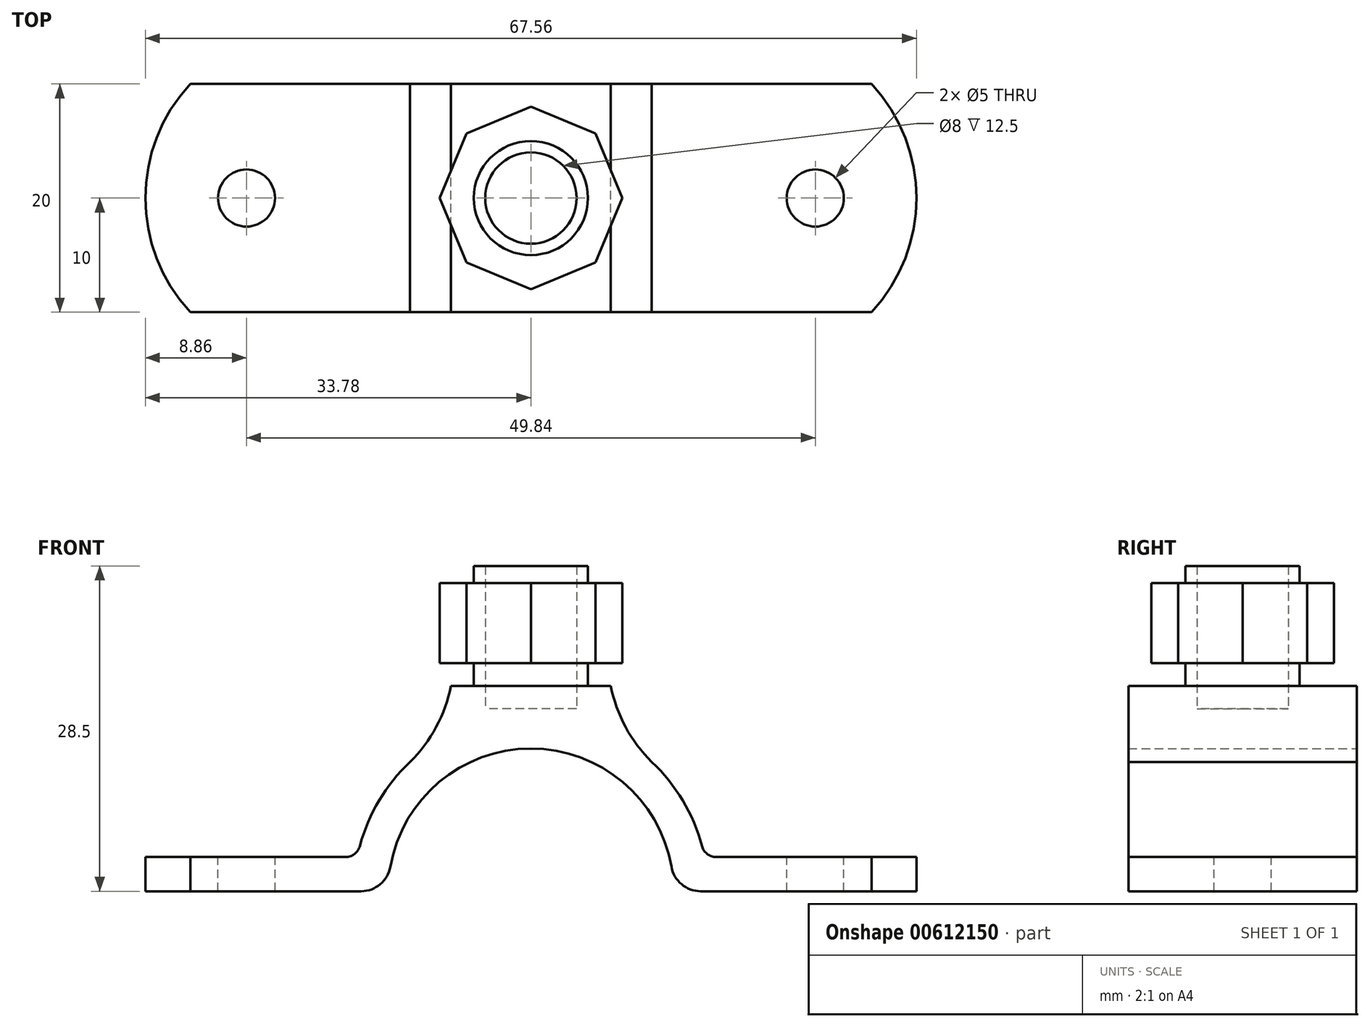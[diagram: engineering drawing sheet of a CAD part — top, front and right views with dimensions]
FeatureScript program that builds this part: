
annotation { "Feature Type Name" : "Feature", "Feature Type Description" : "" }
export const myFeature = defineFeature(function(context is Context, id is Id, definition is map)
    precondition{}
    {
        {
            var Q0;
            Q0=qCreatedBy(makeId("Front.planeOp"),FACE);
            var sketch = newSketch(context, id + "F0", { "sketchPlane" : qUnion([Q0])});
            skArc(sketch, "E0", {"start": v(-10.6, 11.32) * mm, "mid": v(-13.3, 7.95) * mm, "end": v(-14.98, 3.97) * mm});
            skArc(sketch, "E1.0", {"start": v(12.31, 2.15) * mm, "mid": v(0, 12.5) * mm, "end": v(-12.31, 2.15) * mm});
            skLineSegment(sketch, "E2", {"start": v(-14.87, 0) * mm, "end": v(-29.85, 0) * mm});
            skLineSegment(sketch, "E3", {"start": v(-29.85, 0) * mm, "end": v(-29.85, 3) * mm});
            skLineSegment(sketch, "E4", {"start": v(-29.85, 3) * mm, "end": v(-16.24, 3) * mm});
            skLineSegment(sketch, "E5", {"start": v(14.87, 0) * mm, "end": v(29.85, 0) * mm});
            skLineSegment(sketch, "E6", {"start": v(29.85, 0) * mm, "end": v(29.85, 3) * mm});
            skLineSegment(sketch, "E7", {"start": v(29.85, 3) * mm, "end": v(16.24, 3) * mm});
            skLineSegment(sketch, "E8", {"start": v(0, 0) * mm, "end": v(0, 18) * mm, "construction": true});
            skLineSegment(sketch, "E9", {"start": v(-7, 18) * mm, "end": v(7, 18) * mm});
            skArc(sketch, "E10", {"start": v(-10.6, 11.32) * mm, "mid": v(-8.3, 14.4) * mm, "end": v(-7, 18) * mm});
            skArc(sketch, "E11", {"start": v(7, 18) * mm, "mid": v(8.3, 14.4) * mm, "end": v(10.6, 11.32) * mm});
            skArc(sketch, "E12.trimOffspring", {"start": v(14.98, 3.97) * mm, "mid": v(13.3, 7.95) * mm, "end": v(10.6, 11.32) * mm});
            skPoint(sketch, "E13.visualSharp", {"position": v(-15.2, 3) * mm});
            skArc(sketch, "E13.filletArc", {"start": v(-16.24, 3) * mm, "mid": v(-15.45, 3.27) * mm, "end": v(-14.98, 3.97) * mm});
            skPoint(sketch, "E14.visualSharp", {"position": v(15.2, 3) * mm});
            skArc(sketch, "E14.filletArc", {"start": v(14.98, 3.97) * mm, "mid": v(15.45, 3.27) * mm, "end": v(16.24, 3) * mm});
            skPoint(sketch, "E15.visualSharp", {"position": v(-12.5, 0) * mm});
            skArc(sketch, "E15.filletArc", {"start": v(-14.87, 0) * mm, "mid": v(-13.2, 0.6) * mm, "end": v(-12.31, 2.15) * mm});
            skPoint(sketch, "E16.visualSharp", {"position": v(12.5, 0) * mm});
            skArc(sketch, "E16.filletArc", {"start": v(12.31, 2.15) * mm, "mid": v(13.2, 0.6) * mm, "end": v(14.87, 0) * mm});
            skSolve(sketch);
        }
        {
            var Q0;
            Q0=makeQuery(id+"F0.imprint","IMPRINT",FACE,{"disambiguationData":[TD([[makeQuery(id+"F0.imprint","IMPRINT",EDGE,{"derivedFrom":sQuery(id+"F0.wireOp",EDGE,"E0")}),1.0]])]});
            extrude(context, id + "F1", {"entities" : qUnion([Q0]), "endBound" : BoundingType.SYMMETRIC, "depth" : 20 * mm, "offsetDistance" : 25 * mm});
        }
        {
            var Q0;
            Q0=makeQuery(id+"F1.opExtrude","SWEPT_FACE",FACE,{"disambiguationData":[OSD([sQuery(id+"F0.wireOp",EDGE,"E4")])]});
            var sketch = newSketch(context, id + "F2", { "sketchPlane" : qUnion([Q0])});
            skCircle(sketch, "E17", {"center": v(-24.92, 0) * mm, "radius": 2.5 * mm});
            skCircle(sketch, "E18", {"center": v(24.92, 0) * mm, "radius": 2.5 * mm});
            skSolve(sketch);
        }
        {
            var Q0;
            Q0=makeQuery(id+"F2.imprint","IMPRINT",FACE,{"disambiguationData":[TD([[makeQuery(id+"F2.imprint","IMPRINT",EDGE,{"derivedFrom":sQuery(id+"F2.wireOp",EDGE,"E17")}),1.0]])]});
            var Q1;
            Q1=makeQuery(id+"F2.imprint","IMPRINT",FACE,{"disambiguationData":[TD([[makeQuery(id+"F2.imprint","IMPRINT",EDGE,{"derivedFrom":sQuery(id+"F2.wireOp",EDGE,"E18")}),1.0]])]});
            extrude(context, id + "F3", {"entities" : qUnion([Q0, Q1]), "operationType" : NewBodyOperationType.REMOVE, "oppositeDirection" : true, "depth" : 25 * mm, "offsetDistance" : 25 * mm});
        }
        {
            var Q0;
            Q0=makeQuery(id+"F1.opExtrude","SWEPT_FACE",FACE,{"disambiguationData":[OSD([sQuery(id+"F0.wireOp",EDGE,"E4")])]});
            var sketch = newSketch(context, id + "F4", { "sketchPlane" : qUnion([Q0])});
            skArc(sketch, "E19", {"start": v(-29.85, 10) * mm, "mid": v(-33.78, 0) * mm, "end": v(-29.85, -10) * mm});
            skSolve(sketch);
        }
        {
            var Q0;
            Q0=makeQuery(id+"F4.imprint","IMPRINT",FACE,{"disambiguationData":[TD([[makeQuery(id+"F4.imprint","IMPRINT",EDGE,{"derivedFrom":sQuery(id+"F4.wireOp",EDGE,"E19")}),1.0]])]});
            var Q1;
            Q1=makeQuery(id+"F1.opExtrude","SWEPT_FACE",FACE,{"disambiguationData":[OSD([sQuery(id+"F0.wireOp",EDGE,"E2")])]});
            extrude(context, id + "F5", {"entities" : qUnion([Q0]), "operationType" : NewBodyOperationType.ADD, "endBound" : BoundingType.UP_TO_SURFACE, "oppositeDirection" : true, "depth" : 25 * mm, "endBoundEntityFace" : qUnion([Q1]), "offsetDistance" : 25 * mm});
        }
        {
            var Q0;
            Q0=makeQuery(id+"F1.opExtrude","SWEPT_FACE",FACE,{"disambiguationData":[OSD([sQuery(id+"F0.wireOp",EDGE,"E7")])]});
            var sketch = newSketch(context, id + "F6", { "sketchPlane" : qUnion([Q0])});
            skArc(sketch, "E20", {"start": v(29.85, -10) * mm, "mid": v(33.78, 0) * mm, "end": v(29.85, 10) * mm});
            skSolve(sketch);
        }
        {
            var Q0;
            Q0=makeQuery(id+"F6.imprint","IMPRINT",FACE,{"disambiguationData":[TD([[makeQuery(id+"F6.imprint","IMPRINT",EDGE,{"derivedFrom":sQuery(id+"F6.wireOp",EDGE,"E20")}),1.0]])]});
            var Q1;
            Q1=makeQuery(id+"F1.opExtrude","SWEPT_FACE",FACE,{"disambiguationData":[OSD([sQuery(id+"F0.wireOp",EDGE,"E5")])]});
            extrude(context, id + "F7", {"entities" : qUnion([Q0]), "operationType" : NewBodyOperationType.ADD, "endBound" : BoundingType.UP_TO_SURFACE, "oppositeDirection" : true, "depth" : 25 * mm, "endBoundEntityFace" : qUnion([Q1]), "offsetDistance" : 25 * mm});
        }
        {
            var Q0;
            Q0=makeQuery(id+"F1.opExtrude","SWEPT_FACE",FACE,{"disambiguationData":[OSD([sQuery(id+"F0.wireOp",EDGE,"E9")])]});
            var sketch = newSketch(context, id + "F8", { "sketchPlane" : qUnion([Q0])});
            skCircle(sketch, "E21", {"center": v(0, 0) * mm, "radius": 5 * mm});
            skSolve(sketch);
        }
        {
            var Q0;
            Q0 = qSketchRegion(id + "F8", true);
            extrude(context, id + "F9", {"entities" : qUnion([Q0]), "operationType" : NewBodyOperationType.ADD, "depth" : 2 * mm, "offsetDistance" : 25 * mm});
        }
        {
            var Q0;
            Q0=makeQuery(id+"F9.opExtrude","CAP_FACE",FACE,{"disambiguationData":[OSD([sQuery(id+"F8.wireOp",EDGE,"E21")])],"isStart":false});
            var sketch = newSketch(context, id + "F10", { "sketchPlane" : qUnion([Q0])});
            skCircle(sketch, "E22.cCircle", {"center": v(0, 0) * mm, "radius": 8 * mm, "construction": true});
            skLineSegment(sketch, "E22.0", {"start": v(0, -8) * mm, "end": v(-5.66, -5.66) * mm});
            skLineSegment(sketch, "E22.1", {"start": v(-5.66, -5.66) * mm, "end": v(-8, 0) * mm});
            skLineSegment(sketch, "E22.2", {"start": v(-8, 0) * mm, "end": v(-5.66, 5.66) * mm});
            skLineSegment(sketch, "E22.3", {"start": v(-5.66, 5.66) * mm, "end": v(0, 8) * mm});
            skLineSegment(sketch, "E22.4", {"start": v(0, 8) * mm, "end": v(5.66, 5.66) * mm});
            skLineSegment(sketch, "E22.5", {"start": v(5.66, 5.66) * mm, "end": v(8, 0) * mm});
            skLineSegment(sketch, "E22.6", {"start": v(8, 0) * mm, "end": v(5.66, -5.66) * mm});
            skLineSegment(sketch, "E22.7", {"start": v(5.66, -5.66) * mm, "end": v(0, -8) * mm});
            skSolve(sketch);
        }
        {
            var Q0;
            Q0 = qSketchRegion(id + "F10", true);
            extrude(context, id + "F11", {"entities" : qUnion([Q0]), "operationType" : NewBodyOperationType.ADD, "depth" : 7 * mm, "offsetDistance" : 25 * mm});
        }
        {
            var Q0;
            Q0=makeQuery(id+"F11.opExtrude","CAP_FACE",FACE,{"disambiguationData":[OSD([sQuery(id+"F10.wireOp",EDGE,"E22.0"),sQuery(id+"F10.wireOp",EDGE,"E22.1"),sQuery(id+"F10.wireOp",EDGE,"E22.2"),sQuery(id+"F10.wireOp",EDGE,"E22.3"),sQuery(id+"F10.wireOp",EDGE,"E22.4"),sQuery(id+"F10.wireOp",EDGE,"E22.5"),sQuery(id+"F10.wireOp",EDGE,"E22.6"),sQuery(id+"F10.wireOp",EDGE,"E22.7")])],"isStart":false});
            var sketch = newSketch(context, id + "F12", { "sketchPlane" : qUnion([Q0])});
            skCircle(sketch, "E23", {"center": v(0, 0) * mm, "radius": 4 * mm});
            skCircle(sketch, "E24.0", {"center": v(0, 0) * mm, "radius": 5 * mm});
            skSolve(sketch);
        }
        {
            var Q0;
            Q0 = qSketchRegion(id + "F12", true);
            extrude(context, id + "F13", {"entities" : qUnion([Q0]), "operationType" : NewBodyOperationType.ADD, "depth" : 1.5 * mm, "offsetDistance" : 25 * mm});
        }
        {
            var Q0;
            Q0=makeQuery(id+"F13.boolean.opBoolean","SPLIT",FACE,{"disambiguationData":[TD([makeQuery(id+"F13.opExtrude","SWEPT_FACE",FACE,{"disambiguationData":[OSD([sQuery(id+"F12.wireOp",EDGE,"E23")])]})])],"derivedFrom":makeQuery(id+"F11.opExtrude","CAP_FACE",FACE,{"disambiguationData":[OSD([sQuery(id+"F10.wireOp",EDGE,"E22.0"),sQuery(id+"F10.wireOp",EDGE,"E22.1"),sQuery(id+"F10.wireOp",EDGE,"E22.2"),sQuery(id+"F10.wireOp",EDGE,"E22.3"),sQuery(id+"F10.wireOp",EDGE,"E22.4"),sQuery(id+"F10.wireOp",EDGE,"E22.5"),sQuery(id+"F10.wireOp",EDGE,"E22.6"),sQuery(id+"F10.wireOp",EDGE,"E22.7")])],"isStart":false})});
            extrude(context, id + "F14", {"entities" : qUnion([Q0]), "operationType" : NewBodyOperationType.REMOVE, "oppositeDirection" : true, "depth" : 11 * mm, "offsetDistance" : 25 * mm});
        }
    });
